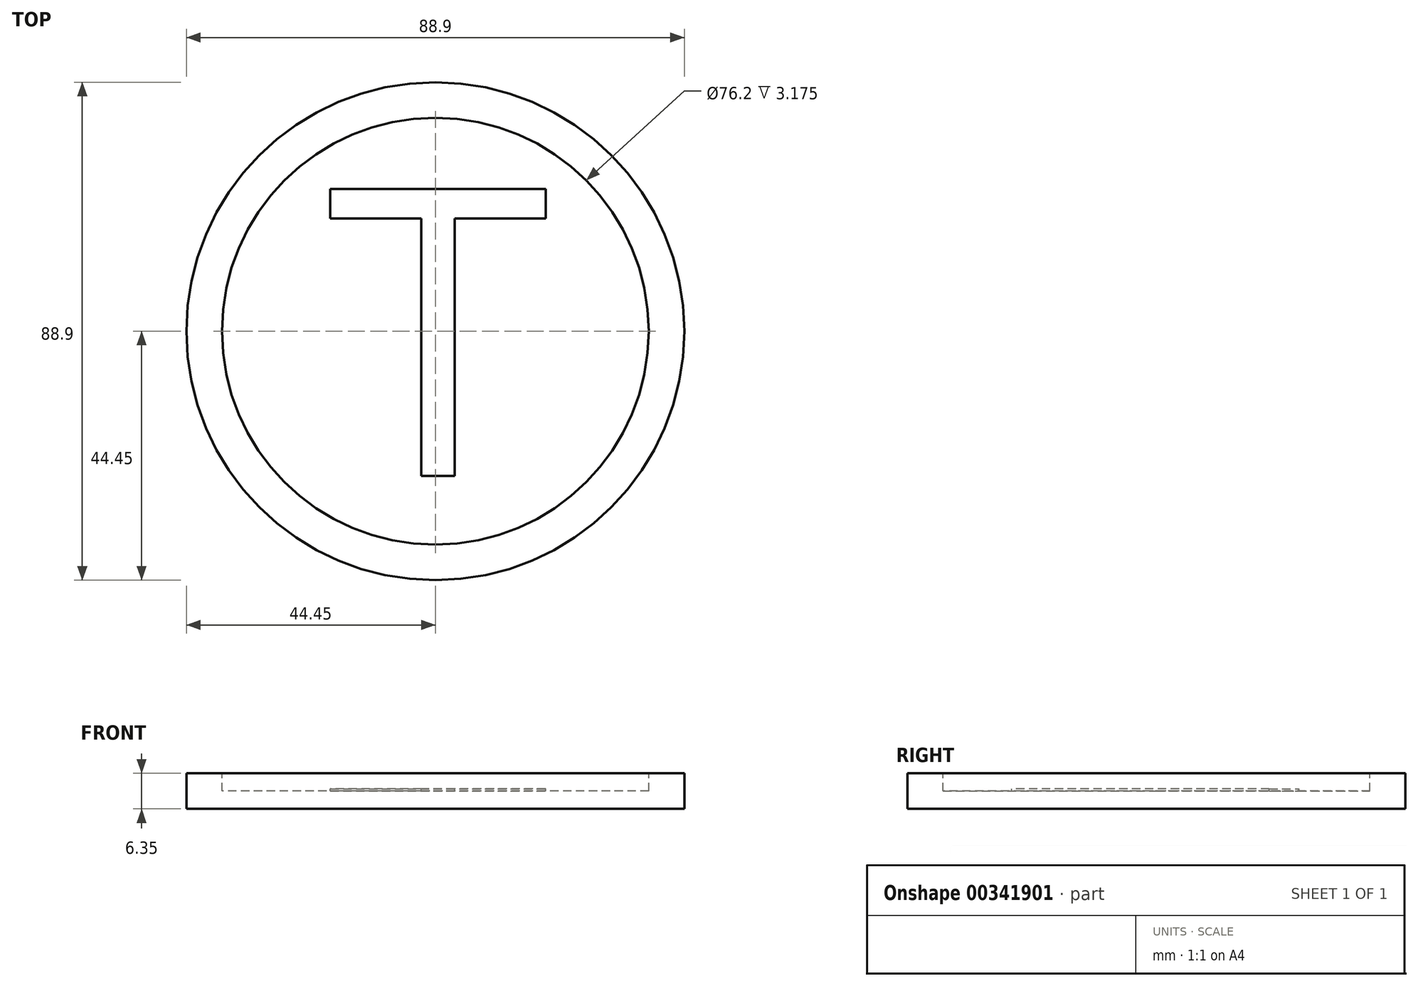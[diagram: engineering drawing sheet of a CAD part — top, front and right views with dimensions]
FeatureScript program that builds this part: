
annotation { "Feature Type Name" : "Feature", "Feature Type Description" : "" }
export const myFeature = defineFeature(function(context is Context, id is Id, definition is map)
    precondition{}
    {
        {
            var Q0;
            Q0=qCreatedBy(makeId("Top.planeOp"),FACE);
            var sketch = newSketch(context, id + "F0", { "sketchPlane" : qUnion([Q0])});
            skCircle(sketch, "E0", {"center": v(0, 0) * mm, "radius": 44.45 * mm});
            skSolve(sketch);
        }
        {
            var Q0;
            Q0=makeQuery(id+"F0.imprint","IMPRINT",FACE,{"disambiguationData":[TD([[makeQuery(id+"F0.imprint","IMPRINT",EDGE,{"derivedFrom":sQuery(id+"F0.wireOp",EDGE,"E0")}),1.0]])]});
            extrude(context, id + "F1", {"entities" : qUnion([Q0]), "depth" : 6.35 * mm});
        }
        {
            var Q0;
            Q0=makeQuery(id+"F1.opExtrude","CAP_FACE",FACE,{"disambiguationData":[OSD([sQuery(id+"F0.wireOp",EDGE,"E0")])],"isStart":false});
            cPlane(context, id + "F2", {"entities" : qUnion([Q0]), "cplaneType" : CPlaneType.OFFSET, "offset" : 0 * mm, "width" : 152.4 * mm, "height" : 152.4 * mm});
        }
        {
            var Q0;
            Q0=qCreatedBy(id+"F2.planeOp",FACE);
            var sketch = newSketch(context, id + "F3", { "sketchPlane" : qUnion([Q0])});
            skCircle(sketch, "E1", {"center": v(0, 0) * mm, "radius": 38.1 * mm});
            skPoint(sketch, "E2", {"position": v(-19.37, -8.08) * mm});
            skPoint(sketch, "E3", {"position": v(-19.37, -25.86) * mm});
            skPoint(sketch, "E4", {"position": v(0, -25.86) * mm});
            skText(sketch, "E5", { "text": "T", "fontName": "OpenSans-Regular.ttf"});
            skPoint(sketch, "E6", {"position": v(-2.5, 20.12) * mm});
            const initialGuessF3  = {"E5": [-0.01937, -0.02586, 1, 0, 0.05172]};
            skSetInitialGuess(sketch, initialGuessF3);
            skSolve(sketch);
        }
        {
            var Q0;
            Q0=makeQuery(id+"F3.imprint","IMPRINT",FACE,{"disambiguationData":[TD([[makeQuery(id+"F3.imprint","IMPRINT",EDGE,{"derivedFrom":sQuery(id+"F3.wireOp",EDGE,"E1")}),1.0]])]});
            var Q1;
            Q1=makeQuery(id+"F3.imprint","IMPRINT",FACE,{"disambiguationData":[TD([[makeQuery(id+"F3.imprint","IMPRINT",EDGE,{"derivedFrom":sQuery(id+"F3.wireOp",EDGE,"da39f52a-e666-4276-ac7f-de5318843af4.sketch_text.stroke-8")}),1.0]])]});
            extrude(context, id + "F4", {"entities" : qUnion([Q0, Q1]), "operationType" : NewBodyOperationType.REMOVE, "oppositeDirection" : true, "depth" : 3.17 * mm});
        }
        {
            var Q0;
            Q0=makeQuery(id+"F3.imprint","IMPRINT",FACE,{"disambiguationData":[TD([[makeQuery(id+"F3.imprint","IMPRINT",EDGE,{"derivedFrom":sQuery(id+"F3.wireOp",EDGE,"E5.sketch_text.stroke-0")}),-1.0]])]});
            extrude(context, id + "F5", {"entities" : qUnion([Q0]), "operationType" : NewBodyOperationType.REMOVE, "oppositeDirection" : true, "depth" : 2.8 * mm});
        }
    });
